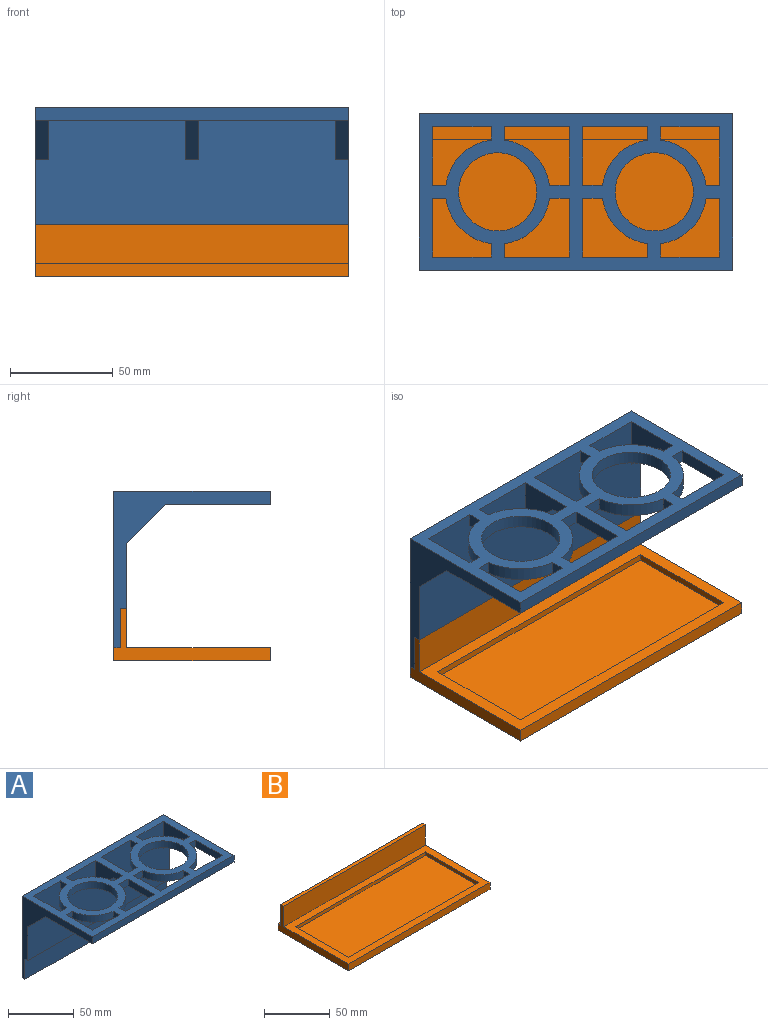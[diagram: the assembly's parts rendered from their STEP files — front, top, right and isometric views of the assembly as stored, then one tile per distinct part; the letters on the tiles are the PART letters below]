
ASSEMBLY  parts=2 mates=1
PART A: 51 faces, bbox 152.4x76.2x76.2 mm
  f0: plane 152.4x69.85mm, normal (0,0,-1), area 3954.3mm2, adj f2,f3,f4,f6,f10,f11,f12,f13
  f1: plane 152.4x76.2mm, normal (0,0,1), area 5284.9mm2, adj f2,f3,f4,f5,f6,f11,f13,f14
  f2: plane 152.4x57.15mm, normal (0,-1,0), area 8145.1mm2, adj f0,f1,f3,f4,f8,f10,f11,f12
  f3: plane 76.2x76.2mm, normal (1,0,0), area 1048.4mm2, adj f0,f1,f2,f5,f6,f7,f8,f9
  f4: plane 76.2x76.2mm, normal (-1,0,0), area 1048.4mm2, adj f0,f1,f2,f5,f6,f7,f8,f9
  f5: plane 152.4x76.2mm, normal (0,1,0), area 11612.9mm2, adj f1,f3,f4,f7
  f6: plane 152.4x6.35mm, normal (0,-1,0), area 967.7mm2, adj f0,f1,f3,f4
  f7: plane 152.4x3.18mm, normal (0,0,-1), area 483.9mm2, adj f3,f4,f5,f9
  f8: plane 152.4x3.18mm, normal (0,0,-1), area 483.9mm2, adj f2,f3,f4,f9
  f9: plane 152.4x19.05mm, normal (0,-1,0), area 2903.2mm2, adj f3,f4,f7,f8
  f10: plane 19.05x19.05mm, normal (0,-0.71,-0.71), area 171.1mm2, adj f0,f2,f4,f11
  f11: plane 28.58x25.4mm, normal (1,0,0), area 362.9mm2, adj f0,f1,f2,f10,f32
  f12: plane 19.05x19.05mm, normal (0,-0.71,-0.71), area 171.1mm2, adj f0,f2,f3,f13
  f13: plane 28.58x25.4mm, normal (-1,0,0), area 362.9mm2, adj f0,f1,f2,f12,f49
  f14: cylinder r=19.05mm len=38.1mm, axis (0,0,1), area 760.1mm2, adj f0,f1
  f15: plane 28.58x6.35mm, normal (-1,0,0), area 181.5mm2, adj f0,f1,f16,f19
  f16: plane 6.55x6.35mm, normal (0,-1,0), area 41.6mm2, adj f0,f1,f15,f17
  f17: cylinder r=25.4mm len=22.03mm, axis (0,0,1), area 212.9mm2, adj f0,f1,f16,f18
  f18: plane 6.55x6.35mm, normal (1,0,0), area 41.6mm2, adj f0,f1,f17,f19
  f19: plane 28.58x6.35mm, normal (0,1,0), area 181.5mm2, adj f0,f1,f15,f18
  f20: cylinder r=25.4mm len=22.03mm, axis (0,0,1), area 212.9mm2, adj f0,f1,f21,f24
  f21: plane 6.55x6.35mm, normal (0,-1,0), area 41.6mm2, adj f0,f1,f20,f22
  f22: plane 28.58x6.35mm, normal (1,0,0), area 181.5mm2, adj f0,f1,f21,f23
  f23: plane 28.58x6.35mm, normal (0,1,0), area 181.5mm2, adj f0,f1,f22,f24
  f24: plane 6.55x6.35mm, normal (-1,0,0), area 41.6mm2, adj f0,f1,f20,f23
  f25: cylinder r=25.4mm len=22.03mm, axis (0,0,1), area 212.9mm2, adj f0,f1,f26,f29
  f26: plane 9.72x6.35mm, normal (0,-1,0), area 61.7mm2, adj f0,f1,f25,f27
  f27: plane 28.58x6.35mm, normal (1,0,0), area 181.5mm2, adj f0,f1,f26,f28
  f28: plane 31.75x6.35mm, normal (0,1,0), area 201.6mm2, adj f0,f1,f27,f29
  f29: plane 6.55x6.35mm, normal (-1,0,0), area 41.6mm2, adj f0,f1,f25,f28
  f30: cylinder r=25.4mm len=22.03mm, axis (0,0,1), area 212.9mm2, adj f0,f1,f31,f32
  f31: plane 6.55x6.35mm, normal (-1,0,0), area 41.6mm2, adj f0,f1,f2,f30
  f32: plane 6.55x6.35mm, normal (0,1,0), area 41.6mm2, adj f0,f1,f11,f30
  f33: cylinder r=19.05mm len=38.1mm, axis (0,0,1), area 760.1mm2, adj f0,f1
  f34: plane 6.55x6.35mm, normal (1,0,0), area 41.6mm2, adj f0,f1,f2,f35
  f35: cylinder r=25.4mm len=22.03mm, axis (0,0,1), area 212.9mm2, adj f0,f1,f34,f36
  f36: plane 9.72x6.35mm, normal (0,1,0), area 61.7mm2, adj f0,f1,f35,f37
  f37: plane 28.58x25.4mm, normal (-1,0,0), area 362.9mm2, adj f0,f1,f2,f36,f50
  f38: plane 9.72x6.35mm, normal (0,-1,0), area 61.7mm2, adj f0,f1,f39,f42
  f39: cylinder r=25.4mm len=22.03mm, axis (0,0,1), area 212.9mm2, adj f0,f1,f38,f40
  f40: plane 6.55x6.35mm, normal (1,0,0), area 41.6mm2, adj f0,f1,f39,f41
  f41: plane 31.75x6.35mm, normal (0,1,0), area 201.6mm2, adj f0,f1,f40,f42
  f42: plane 28.58x6.35mm, normal (-1,0,0), area 181.5mm2, adj f0,f1,f38,f41
  f43: plane 9.72x6.35mm, normal (0,1,0), area 61.7mm2, adj f0,f1,f44,f46
  f44: cylinder r=25.4mm len=22.03mm, axis (0,0,1), area 212.9mm2, adj f0,f1,f43,f45
  f45: plane 6.55x6.35mm, normal (-1,0,0), area 41.6mm2, adj f0,f1,f2,f44
  f46: plane 28.58x25.4mm, normal (1,0,0), area 362.9mm2, adj f0,f1,f2,f43,f50
  f47: plane 6.55x6.35mm, normal (1,0,0), area 41.6mm2, adj f0,f1,f2,f48
  f48: cylinder r=25.4mm len=22.03mm, axis (0,0,1), area 212.9mm2, adj f0,f1,f47,f49
  f49: plane 6.55x6.35mm, normal (0,1,0), area 41.6mm2, adj f0,f1,f13,f48
  f50: plane 19.05x19.05mm, normal (0,-0.71,-0.71), area 171.1mm2, adj f0,f2,f37,f46
PART B: 15 faces, bbox 152.4x76.2x25.4 mm
  f0: plane 152.4x76.2mm, normal (0,0,-1), area 11612.9mm2, adj f1,f7,f8,f9
  f1: plane 152.4x6.35mm, normal (0,1,0), area 967.7mm2, adj f0,f2,f8,f9
  f2: plane 152.4x3.18mm, normal (0,0,1), area 483.9mm2, adj f1,f3,f8,f9
  f3: plane 152.4x19.05mm, normal (0,1,0), area 2903.2mm2, adj f2,f4,f8,f9
  f4: plane 152.4x3.18mm, normal (0,0,1), area 483.9mm2, adj f3,f5,f8,f9
  f5: plane 152.4x19.05mm, normal (0,-1,0), area 2903.2mm2, adj f4,f6,f8,f9
  f6: plane 152.4x69.85mm, normal (0,0,1), area 2661.3mm2, adj f5,f7,f8,f9,f10,f11,f12,f13
  f7: plane 152.4x6.35mm, normal (0,-1,0), area 967.7mm2, adj f0,f6,f8,f9
  f8: plane 76.2x25.4mm, normal (1,0,0), area 544.4mm2, adj f0,f1,f2,f3,f4,f5,f6,f7
  f9: plane 76.2x25.4mm, normal (-1,0,0), area 544.4mm2, adj f0,f1,f2,f3,f4,f5,f6,f7
  f10: plane 57.15x3.18mm, normal (-1,0,0), area 181.5mm2, adj f6,f11,f13,f14
  f11: plane 139.7x3.18mm, normal (0,-1,0), area 443.5mm2, adj f6,f10,f12,f14
  f12: plane 57.15x3.18mm, normal (1,0,0), area 181.5mm2, adj f6,f11,f13,f14
  f13: plane 139.7x3.18mm, normal (0,1,0), area 443.5mm2, adj f6,f10,f12,f14
  f14: plane 139.7x57.15mm, normal (0,0,1), area 7983.9mm2, adj f10,f11,f12,f13
PLACE A t=(-44.87,-5.16,24.77)mm
PLACE B t=(-121.07,32.94,18.42)mm
MATE fastened A.f9 <-> B.f3  axis (0,-1,0) through (-121.07,29.76,24.77)mm
